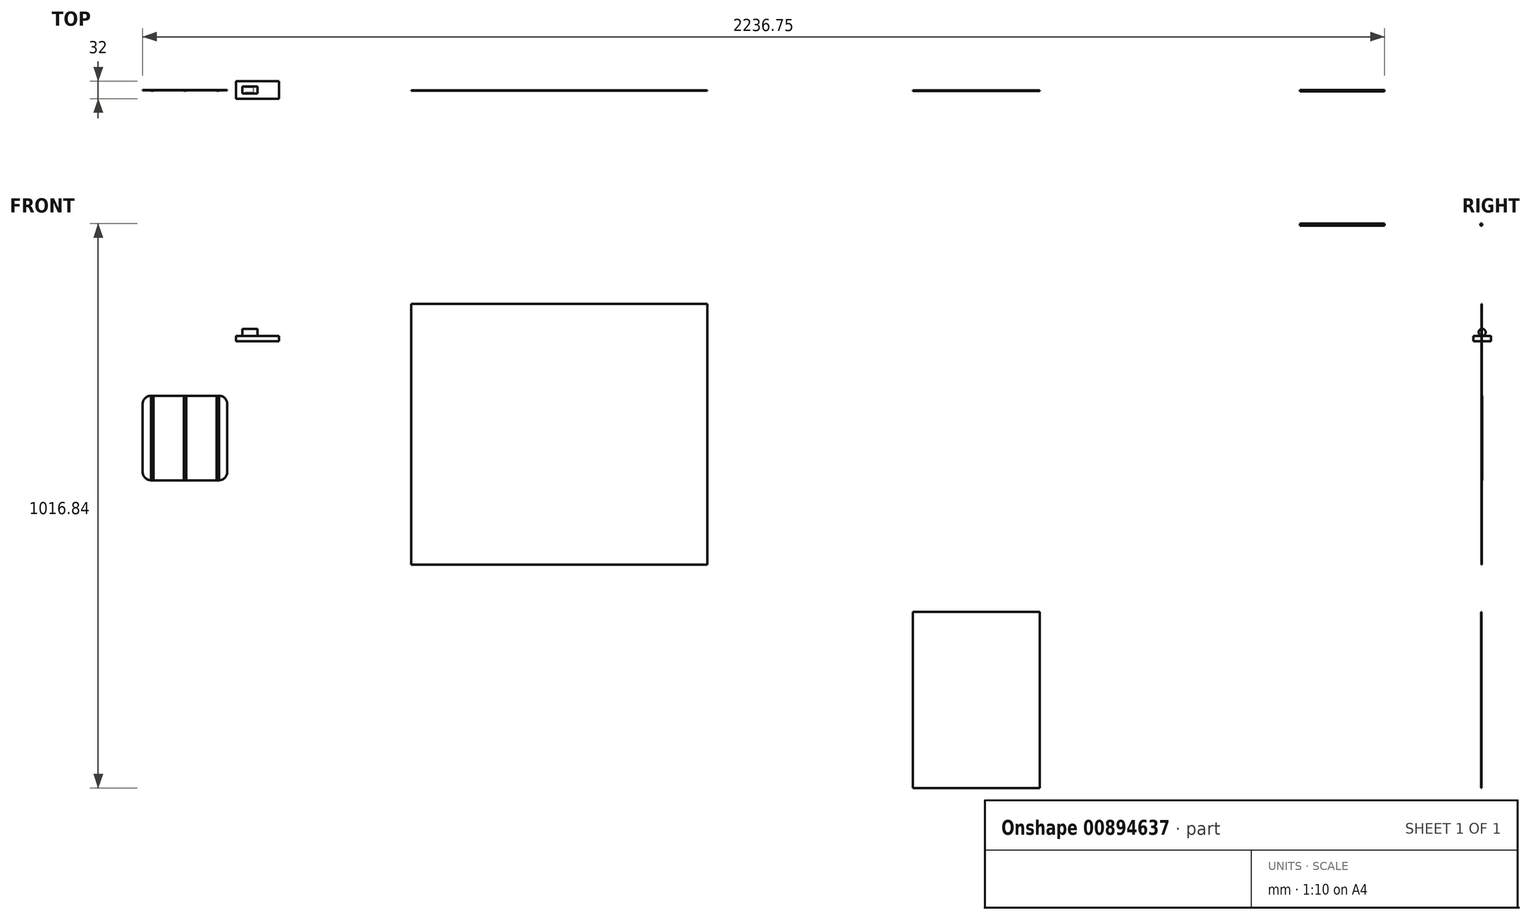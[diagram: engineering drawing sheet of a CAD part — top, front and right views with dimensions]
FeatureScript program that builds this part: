
annotation { "Feature Type Name" : "Feature", "Feature Type Description" : "" }
export const myFeature = defineFeature(function(context is Context, id is Id, definition is map)
    precondition{}
    {
        {
            var Q0;
            Q0=qCreatedBy(makeId("Front.planeOp"),FACE);
            var sketch = newSketch(context, id + "F0", { "sketchPlane" : qUnion([Q0])});
            skLineSegment(sketch, "E0.bottom", {"start": v(766.3, 678.17) * mm, "end": v(888.7, 678.17) * mm});
            skLineSegment(sketch, "E0.top", {"start": v(766.3, 525.77) * mm, "end": v(888.7, 525.77) * mm});
            skLineSegment(sketch, "E0.left", {"start": v(751.3, 663.17) * mm, "end": v(751.3, 540.77) * mm});
            skLineSegment(sketch, "E0.right", {"start": v(903.7, 663.17) * mm, "end": v(903.7, 540.77) * mm});
            skPoint(sketch, "E1.visualSharp", {"position": v(751.3, 678.17) * mm});
            skArc(sketch, "E1.filletArc", {"start": v(766.3, 678.17) * mm, "mid": v(755.7, 673.78) * mm, "end": v(751.3, 663.17) * mm});
            skPoint(sketch, "E2.visualSharp", {"position": v(903.7, 678.17) * mm});
            skArc(sketch, "E2.filletArc", {"start": v(903.7, 663.17) * mm, "mid": v(899.3, 673.78) * mm, "end": v(888.7, 678.17) * mm});
            skPoint(sketch, "E3.visualSharp", {"position": v(903.7, 525.77) * mm});
            skArc(sketch, "E3.filletArc", {"start": v(888.7, 525.77) * mm, "mid": v(899.3, 530.16) * mm, "end": v(903.7, 540.77) * mm});
            skPoint(sketch, "E4.visualSharp", {"position": v(751.3, 525.77) * mm});
            skArc(sketch, "E4.filletArc", {"start": v(751.3, 540.77) * mm, "mid": v(755.7, 530.16) * mm, "end": v(766.3, 525.77) * mm});
            skLineSegment(sketch, "E5.bottom", {"start": v(3038.85, 81858.35) * mm, "end": v(2869.38, 81858.35) * mm});
            skLineSegment(sketch, "E5.top", {"start": v(3038.85, 72650.5) * mm, "end": v(2869.38, 72650.5) * mm});
            skLineSegment(sketch, "E5.left", {"start": v(3038.85, 81858.35) * mm, "end": v(3038.85, 72650.5) * mm});
            skLineSegment(sketch, "E5.right", {"start": v(2869.38, 81858.35) * mm, "end": v(2869.38, 72650.5) * mm});
            skSolve(sketch);
        }
        {
            var Q0;
            Q0=makeQuery(id+"F0.imprint","IMPRINT",FACE,{"disambiguationData":[TD([[makeQuery(id+"F0.imprint","IMPRINT",EDGE,{"derivedFrom":sQuery(id+"F0.wireOp",EDGE,"E0.bottom")}),-1.0]])]});
            extrude(context, id + "F1", {"entities" : qUnion([Q0]), "depth" : 1 * mm, "offsetDistance" : 25 * mm});
        }
        {
            var Q0;
            Q0=makeQuery(id+"F1.opExtrude","CAP_FACE",FACE,{"disambiguationData":[OSD([sQuery(id+"F0.wireOp",EDGE,"E0.bottom"),sQuery(id+"F0.wireOp",EDGE,"E0.top"),sQuery(id+"F0.wireOp",EDGE,"E0.left"),sQuery(id+"F0.wireOp",EDGE,"E0.right"),sQuery(id+"F0.wireOp",EDGE,"E1.filletArc"),sQuery(id+"F0.wireOp",EDGE,"E2.filletArc"),sQuery(id+"F0.wireOp",EDGE,"E3.filletArc"),sQuery(id+"F0.wireOp",EDGE,"E4.filletArc")])],"isStart":false});
            var sketch = newSketch(context, id + "F2", { "sketchPlane" : qUnion([Q0])});
            skLineSegment(sketch, "E6.bottom", {"start": v(1067.58, 689.47) * mm, "end": v(1071.78, 689.47) * mm});
            skLineSegment(sketch, "E6.top", {"start": v(1067.58, 537.07) * mm, "end": v(1071.78, 537.07) * mm});
            skLineSegment(sketch, "E6.left", {"start": v(1067.58, 689.47) * mm, "end": v(1067.58, 537.07) * mm});
            skLineSegment(sketch, "E6.right", {"start": v(1071.78, 689.47) * mm, "end": v(1071.78, 537.07) * mm});
            skLineSegment(sketch, "E7.bottom", {"start": v(1040.2, 697.09) * mm, "end": v(1044.38, 697.09) * mm});
            skLineSegment(sketch, "E7.top", {"start": v(1040.2, 544.69) * mm, "end": v(1044.38, 544.69) * mm});
            skLineSegment(sketch, "E7.left", {"start": v(1040.2, 697.09) * mm, "end": v(1040.2, 544.69) * mm});
            skLineSegment(sketch, "E7.right", {"start": v(1044.38, 697.09) * mm, "end": v(1044.38, 544.69) * mm});
            skLineSegment(sketch, "E8.bottom", {"start": v(998.8, 676.8) * mm, "end": v(1003, 676.8) * mm});
            skLineSegment(sketch, "E8.top", {"start": v(998.8, 524.4) * mm, "end": v(1003, 524.4) * mm});
            skLineSegment(sketch, "E8.left", {"start": v(998.8, 676.8) * mm, "end": v(998.8, 524.4) * mm});
            skLineSegment(sketch, "E8.right", {"start": v(1003, 676.8) * mm, "end": v(1003, 524.4) * mm});
            skSolve(sketch);
        }
        {
            var Q0;
            Q0=makeQuery(id+"F2.imprint","IMPRINT",FACE,{"disambiguationData":[TD([[makeQuery(id+"F2.imprint","IMPRINT",EDGE,{"derivedFrom":sQuery(id+"F2.wireOp",EDGE,"E6.bottom")}),-1.0]])]});
            var Q1;
            Q1=makeQuery(id+"F2.imprint","IMPRINT",FACE,{"disambiguationData":[TD([[makeQuery(id+"F2.imprint","IMPRINT",EDGE,{"derivedFrom":sQuery(id+"F2.wireOp",EDGE,"E7.bottom")}),-1.0]])]});
            var Q2;
            Q2=makeQuery(id+"F2.imprint","IMPRINT",FACE,{"disambiguationData":[TD([[makeQuery(id+"F2.imprint","IMPRINT",EDGE,{"derivedFrom":sQuery(id+"F2.wireOp",EDGE,"E8.bottom")}),-1.0]])]});
            extrude(context, id + "F3", {"entities" : qUnion([Q0, Q1, Q2]), "depth" : 0.5 * mm, "offsetDistance" : 25 * mm});
        }
        {
            var Q0;
            Q0=makeQuery(id+"F3.opExtrude","SWEPT_BODY",BODY,{"disambiguationData":[OSD([sQuery(id+"F2.wireOp",EDGE,"E8.bottom"),sQuery(id+"F2.wireOp",EDGE,"E8.top"),sQuery(id+"F2.wireOp",EDGE,"E8.left"),sQuery(id+"F2.wireOp",EDGE,"E8.right")])]});
            transform(context, id + "F4", {"entities" : qUnion([Q0]), "transformType" : TransformType.TRANSLATION_3D, "dx" : -232.8 * mm, "dy" : 0 * mm, "dz" : 3.3 * mm, "makeCopy" : false});
        }
        {
            var Q0;
            Q0=makeQuery(id+"F3.opExtrude","SWEPT_BODY",BODY,{"disambiguationData":[OSD([sQuery(id+"F2.wireOp",EDGE,"E8.bottom"),sQuery(id+"F2.wireOp",EDGE,"E8.top"),sQuery(id+"F2.wireOp",EDGE,"E8.left"),sQuery(id+"F2.wireOp",EDGE,"E8.right")])]});
            transform(context, id + "F5", {"entities" : qUnion([Q0]), "transformType" : TransformType.TRANSLATION_3D, "dx" : 6E-4000 * mm, "dy" : 0 * mm, "dz" : 0 * mm, "makeCopy" : false});
        }
        {
            var Q0;
            Q0=makeQuery(id+"F3.opExtrude","SWEPT_BODY",BODY,{"disambiguationData":[OSD([sQuery(id+"F2.wireOp",EDGE,"E8.bottom"),sQuery(id+"F2.wireOp",EDGE,"E8.top"),sQuery(id+"F2.wireOp",EDGE,"E8.left"),sQuery(id+"F2.wireOp",EDGE,"E8.right")])]});
            var Q1;
            Q1=makeQuery(id+"F3.opExtrude","CAP_VERTEX",VERTEX,{"disambiguationData":[OSD([sQuery(id+"F2.wireOp",EDGE,"E8.top"),sQuery(id+"F2.wireOp",EDGE,"E8.left")])],"isStart":false});
            var Q2;
            Q2=makeQuery(id+"F1.opExtrude","CAP_EDGE",EDGE,{"disambiguationData":[OSD([sQuery(id+"F0.wireOp",EDGE,"E0.top")])],"isStart":false});
            transform(context, id + "F6", {"entities" : qUnion([Q0]), "transformType" : TransformType.TRANSLATION_ENTITY, "oppositeDirectionEntity" : false, "transformLine" : qUnion([Q1, Q2]), "makeCopy" : false});
        }
        {
            var Q0;
            Q0=makeQuery(id+"F3.opExtrude","SWEPT_BODY",BODY,{"disambiguationData":[OSD([sQuery(id+"F2.wireOp",EDGE,"E8.bottom"),sQuery(id+"F2.wireOp",EDGE,"E8.top"),sQuery(id+"F2.wireOp",EDGE,"E8.left"),sQuery(id+"F2.wireOp",EDGE,"E8.right")])]});
            var Q1;
            Q1=makeQuery(id+"F3.opExtrude","CAP_VERTEX",VERTEX,{"disambiguationData":[OSD([sQuery(id+"F2.wireOp",EDGE,"E8.bottom"),sQuery(id+"F2.wireOp",EDGE,"E8.right")])],"isStart":true});
            var Q2;
            Q2=makeQuery(id+"F1.opExtrude","CAP_VERTEX",VERTEX,{"disambiguationData":[OSD([sQuery(id+"F0.wireOp",EDGE,"E0.bottom"),sQuery(id+"F0.wireOp",EDGE,"E2.filletArc")])],"isStart":false});
            transform(context, id + "F7", {"entities" : qUnion([Q0]), "transformType" : TransformType.TRANSLATION_ENTITY, "oppositeDirectionEntity" : false, "transformLine" : qUnion([Q1, Q2]), "makeCopy" : false});
        }
        {
            var Q0;
            Q0=makeQuery(id+"F3.opExtrude","SWEPT_BODY",BODY,{"disambiguationData":[OSD([sQuery(id+"F2.wireOp",EDGE,"E7.bottom"),sQuery(id+"F2.wireOp",EDGE,"E7.top"),sQuery(id+"F2.wireOp",EDGE,"E7.left"),sQuery(id+"F2.wireOp",EDGE,"E7.right")])]});
            var Q1;
            Q1=sQuery(id+"F2.wireOp",VERTEX,"E7.bottom.start");
            var Q2;
            Q2=makeQuery(id+"F1.opExtrude","CAP_VERTEX",VERTEX,{"disambiguationData":[OSD([sQuery(id+"F0.wireOp",EDGE,"E0.bottom"),sQuery(id+"F0.wireOp",EDGE,"E1.filletArc")])],"isStart":false});
            transform(context, id + "F8", {"entities" : qUnion([Q0]), "transformType" : TransformType.TRANSLATION_ENTITY, "oppositeDirectionEntity" : false, "transformLine" : qUnion([Q1, Q2]), "makeCopy" : false});
        }
        {
            var Q0;
            Q0=sQuery(id+"F2.wireOp",EDGE,"E6.bottom");
            cPoint(context, id + "F9", {"entities" : qUnion([Q0]), "parameter" : 0.5});
        }
        {
            var Q0;
            Q0=makeQuery(id+"F1.opExtrude","CAP_EDGE",EDGE,{"disambiguationData":[OSD([sQuery(id+"F0.wireOp",EDGE,"E0.bottom")])],"isStart":false});
            cPoint(context, id + "F10", {"entities" : qUnion([Q0]), "parameter" : 0.5});
        }
        {
            var Q0;
            Q0=makeQuery(id+"F3.opExtrude","SWEPT_BODY",BODY,{"disambiguationData":[OSD([sQuery(id+"F2.wireOp",EDGE,"E6.bottom"),sQuery(id+"F2.wireOp",EDGE,"E6.top"),sQuery(id+"F2.wireOp",EDGE,"E6.left"),sQuery(id+"F2.wireOp",EDGE,"E6.right")])]});
            var Q1;
            Q1=qCreatedBy(id+"F9",VERTEX);
            var Q2;
            Q2=qCreatedBy(id+"F10",VERTEX);
            transform(context, id + "F11", {"entities" : qUnion([Q0]), "transformType" : TransformType.TRANSLATION_ENTITY, "oppositeDirectionEntity" : false, "transformLine" : qUnion([Q1, Q2]), "makeCopy" : false});
        }
        {
            var Q0;
            Q0=qCreatedBy(makeId("Front.planeOp"),FACE);
            var sketch = newSketch(context, id + "F12", { "sketchPlane" : qUnion([Q0])});
            skLineSegment(sketch, "E9.bottom", {"start": v(919.16, 786.05) * mm, "end": v(997.16, 786.05) * mm});
            skLineSegment(sketch, "E9.top", {"start": v(919.16, 776.05) * mm, "end": v(997.16, 776.05) * mm});
            skLineSegment(sketch, "E9.left", {"start": v(919.16, 786.05) * mm, "end": v(919.16, 776.05) * mm});
            skLineSegment(sketch, "E9.right", {"start": v(997.16, 786.05) * mm, "end": v(997.16, 776.05) * mm});
            skPoint(sketch, "E10.oppositeSnap0", {"position": v(958.16, 786.05) * mm});
            skLineSegment(sketch, "E10.bottom", {"start": v(997.16, 786.05) * mm, "end": v(958.16, 786.05) * mm});
            skLineSegment(sketch, "E10.top", {"start": v(997.16, 798.75) * mm, "end": v(958.16, 798.75) * mm});
            skLineSegment(sketch, "E10.left", {"start": v(997.16, 786.05) * mm, "end": v(997.16, 798.75) * mm});
            skLineSegment(sketch, "E10.right", {"start": v(958.16, 786.05) * mm, "end": v(958.16, 798.75) * mm});
            skLineSegment(sketch, "E11.bottom", {"start": v(958.16, 792.4) * mm, "end": v(930.77, 792.4) * mm});
            skLineSegment(sketch, "E11.top", {"start": v(958.16, 786.05) * mm, "end": v(930.77, 786.05) * mm});
            skLineSegment(sketch, "E11.left", {"start": v(958.16, 792.4) * mm, "end": v(958.16, 786.05) * mm});
            skLineSegment(sketch, "E11.right", {"start": v(930.77, 792.4) * mm, "end": v(930.77, 786.05) * mm});
            skSolve(sketch);
        }
        {
            var Q0;
            Q0=makeQuery(id+"F12.imprint","IMPRINT",FACE,{"disambiguationData":[TD([[makeQuery(id+"F12.imprint","IMPRINT",EDGE,{"derivedFrom":sQuery(id+"F12.wireOp",EDGE,"E10.bottom")}),-1.0]])]});
            var Q1;
            Q1=makeQuery(id+"F12.imprint","IMPRINT",FACE,{"disambiguationData":[TD([[makeQuery(id+"F12.imprint","IMPRINT",EDGE,{"derivedFrom":sQuery(id+"F12.wireOp",EDGE,"E9.bottom")}),-1.0]])]});
            extrude(context, id + "F13", {"entities" : qUnion([Q0, Q1]), "endBound" : BoundingType.SYMMETRIC, "depth" : 32 * mm, "offsetDistance" : 25 * mm});
        }
        {
            var Q0;
            Q0=makeQuery(id+"F12.imprint","IMPRINT",FACE,{"disambiguationData":[TD([[makeQuery(id+"F12.imprint","IMPRINT",EDGE,{"derivedFrom":sQuery(id+"F12.wireOp",EDGE,"E11.bottom")}),1.0]])]});
            var Q1;
            Q1=sQuery(id+"F12.wireOp",EDGE,"E11.bottom");
            revolve(context, id + "F14", {"surfaceOperationType" : NewSurfaceOperationType.NEW, "entities" : qUnion([Q0]), "axis" : qUnion([Q1]), "revolveType" : RevolveType.ONE_DIRECTION, "angle" : 360 * degree});
        }
        {
            var Q0;
            Q0=makeQuery(id+"F14.opRevolve","SWEPT_FACE",FACE,{"disambiguationData":[OSD([sQuery(id+"F12.wireOp",EDGE,"E11.right")])]});
            var sketch = newSketch(context, id + "F15", { "sketchPlane" : qUnion([Q0])});
            skCircle(sketch, "E12", {"center": v(0, 792.4) * mm, "radius": 7.66 * mm});
            skSolve(sketch);
        }
        {
            var Q0;
            Q0=makeQuery(id+"F15.imprint","IMPRINT",FACE,{"disambiguationData":[TD([[makeQuery(id+"F15.imprint","IMPRINT",EDGE,{"derivedFrom":sQuery(id+"F15.wireOp",EDGE,"E12")}),1.0]])]});
            extrude(context, id + "F16", {"entities" : qUnion([Q0]), "operationType" : NewBodyOperationType.REMOVE, "depth" : -20 * mm, "offsetDistance" : 25 * mm});
        }
        {
            var Q0;
            Q0=makeQuery(id+"F1.opExtrude","CAP_FACE",FACE,{"disambiguationData":[OSD([sQuery(id+"F0.wireOp",EDGE,"E0.bottom"),sQuery(id+"F0.wireOp",EDGE,"E0.top"),sQuery(id+"F0.wireOp",EDGE,"E0.left"),sQuery(id+"F0.wireOp",EDGE,"E0.right"),sQuery(id+"F0.wireOp",EDGE,"E1.filletArc"),sQuery(id+"F0.wireOp",EDGE,"E2.filletArc"),sQuery(id+"F0.wireOp",EDGE,"E3.filletArc"),sQuery(id+"F0.wireOp",EDGE,"E4.filletArc")])],"isStart":false});
            var sketch = newSketch(context, id + "F17", { "sketchPlane" : qUnion([Q0])});
            skLineSegment(sketch, "E13.bottom", {"start": v(1234.72, 843.78) * mm, "end": v(1768.12, 843.78) * mm});
            skLineSegment(sketch, "E13.top", {"start": v(1234.72, 373.88) * mm, "end": v(1768.12, 373.88) * mm});
            skLineSegment(sketch, "E13.left", {"start": v(1234.72, 843.78) * mm, "end": v(1234.72, 373.88) * mm});
            skLineSegment(sketch, "E13.right", {"start": v(1768.12, 843.78) * mm, "end": v(1768.12, 373.88) * mm});
            skSolve(sketch);
        }
        {
            var Q0;
            Q0=makeQuery(id+"F17.imprint","IMPRINT",FACE,{"disambiguationData":[TD([[makeQuery(id+"F17.imprint","IMPRINT",EDGE,{"derivedFrom":sQuery(id+"F17.wireOp",EDGE,"E13.bottom")}),-1.0]])]});
            extrude(context, id + "F18", {"entities" : qUnion([Q0]), "endBound" : BoundingType.SYMMETRIC, "depth" : 1 * mm, "offsetDistance" : 25.4 * mm});
        }
        {
            var Q0;
            Q0=makeQuery(id+"F18.opExtrude","CAP_FACE",FACE,{"disambiguationData":[OSD([sQuery(id+"F17.wireOp",EDGE,"E13.bottom"),sQuery(id+"F17.wireOp",EDGE,"E13.top"),sQuery(id+"F17.wireOp",EDGE,"E13.left"),sQuery(id+"F17.wireOp",EDGE,"E13.right")])],"isStart":false});
            var sketch = newSketch(context, id + "F19", { "sketchPlane" : qUnion([Q0])});
            skLineSegment(sketch, "E14.bottom", {"start": v(2175.25, 988.19) * mm, "end": v(2988.05, 988.19) * mm});
            skLineSegment(sketch, "E14.top", {"start": v(2175.25, 505.59) * mm, "end": v(2988.05, 505.59) * mm});
            skLineSegment(sketch, "E14.left", {"start": v(2175.25, 988.19) * mm, "end": v(2175.25, 505.59) * mm});
            skLineSegment(sketch, "E14.right", {"start": v(2988.05, 988.19) * mm, "end": v(2988.05, 505.59) * mm});
            skLineSegment(sketch, "E15.bottom", {"start": v(2988.05, 988.19) * mm, "end": v(2835.65, 988.19) * mm});
            skLineSegment(sketch, "E15.top", {"start": v(2988.05, 835.79) * mm, "end": v(2835.65, 835.79) * mm});
            skLineSegment(sketch, "E15.left", {"start": v(2988.05, 988.19) * mm, "end": v(2988.05, 835.79) * mm});
            skLineSegment(sketch, "E15.right", {"start": v(2835.65, 988.19) * mm, "end": v(2835.65, 835.79) * mm});
            skLineSegment(sketch, "E16.bottom", {"start": v(2988.05, 835.79) * mm, "end": v(2984.25, 835.79) * mm});
            skLineSegment(sketch, "E16.top", {"start": v(2988.05, 988.19) * mm, "end": v(2984.25, 988.19) * mm});
            skLineSegment(sketch, "E16.left", {"start": v(2988.05, 835.79) * mm, "end": v(2988.05, 988.19) * mm});
            skLineSegment(sketch, "E16.right", {"start": v(2984.25, 835.79) * mm, "end": v(2984.25, 988.19) * mm});
            skLineSegment(sketch, "E17.bottom", {"start": v(2835.65, 988.19) * mm, "end": v(2988.05, 988.19) * mm});
            skLineSegment(sketch, "E17.top", {"start": v(2835.65, 984.43) * mm, "end": v(2988.05, 984.43) * mm});
            skLineSegment(sketch, "E17.left", {"start": v(2835.65, 988.19) * mm, "end": v(2835.65, 984.43) * mm});
            skLineSegment(sketch, "E17.right", {"start": v(2988.05, 988.19) * mm, "end": v(2988.05, 984.43) * mm});
            skSolve(sketch);
        }
        {
            var Q0;
            Q0=makeQuery(id+"F19.imprint","IMPRINT",FACE,{"disambiguationData":[TD([[makeQuery(id+"F19.imprint","IMPRINT",EDGE,{"derivedFrom":sQuery(id+"F19.wireOp",EDGE,"E14.bottom")}),-1.0]])]});
            var Q1;
            {var subQ5=sQuery(id+"F19.wireOp",EDGE,"E17.left");Q1=makeQuery(id+"F19.imprint","IMPRINT",FACE,{"disambiguationData":[TD([[makeQuery(id+"F19.imprint","IMPRINT",EDGE,{"derivedFrom":subQ5}),1.0]])]});}
            var Q2;
            {var subQ5=sQuery(id+"F19.wireOp",EDGE,"E17.right");Q2=makeQuery(id+"F19.imprint","IMPRINT",FACE,{"disambiguationData":[TD([[makeQuery(id+"F19.imprint","IMPRINT",EDGE,{"derivedFrom":subQ5}),-1.0]])]});}
            var Q3;
            {var subQ0=sQuery(id+"F19.wireOp",EDGE,"E16.bottom");Q3=makeQuery(id+"F19.imprint","IMPRINT",FACE,{"disambiguationData":[TD([[makeQuery(id+"F19.imprint","IMPRINT",EDGE,{"derivedFrom":subQ0}),-1.0]])]});}
            extrude(context, id + "F20", {"entities" : qUnion([Q0, Q1, Q2, Q3]), "endBound" : BoundingType.SYMMETRIC, "depth" : 2.66 * mm, "offsetDistance" : 25.4 * mm});
        }
        {
            var Q0;
            Q0=makeQuery(id+"F18.opExtrude","CAP_FACE",FACE,{"disambiguationData":[OSD([sQuery(id+"F17.wireOp",EDGE,"E13.bottom"),sQuery(id+"F17.wireOp",EDGE,"E13.top"),sQuery(id+"F17.wireOp",EDGE,"E13.left"),sQuery(id+"F17.wireOp",EDGE,"E13.right")])],"isStart":false});
            var sketch = newSketch(context, id + "F21", { "sketchPlane" : qUnion([Q0])});
            skLineSegment(sketch, "E18.bottom", {"start": v(2138.3, 288.85) * mm, "end": v(2366.9, 288.85) * mm});
            skLineSegment(sketch, "E18.top", {"start": v(2138.3, -28.65) * mm, "end": v(2366.9, -28.65) * mm});
            skLineSegment(sketch, "E18.left", {"start": v(2138.3, 288.85) * mm, "end": v(2138.3, -28.65) * mm});
            skLineSegment(sketch, "E18.right", {"start": v(2366.9, 288.85) * mm, "end": v(2366.9, -28.65) * mm});
            skSolve(sketch);
        }
        {
            var Q0;
            Q0=makeQuery(id+"F21.imprint","IMPRINT",FACE,{"disambiguationData":[TD([[makeQuery(id+"F21.imprint","IMPRINT",EDGE,{"derivedFrom":sQuery(id+"F21.wireOp",EDGE,"E18.bottom")}),-1.0]])]});
            extrude(context, id + "F22", {"entities" : qUnion([Q0]), "endBound" : BoundingType.SYMMETRIC, "depth" : 1 * mm, "offsetDistance" : 25.4 * mm});
        }
    });
